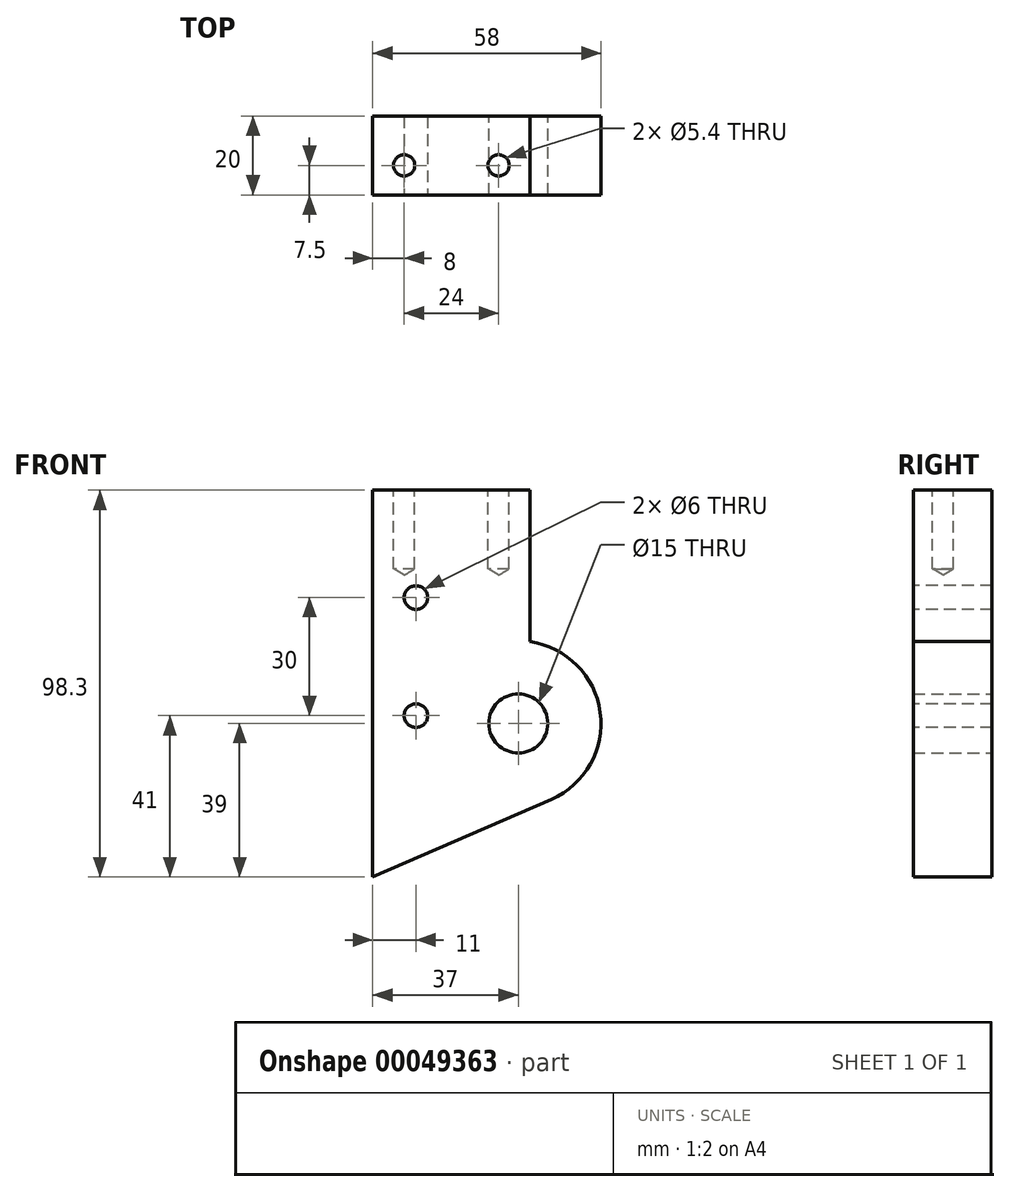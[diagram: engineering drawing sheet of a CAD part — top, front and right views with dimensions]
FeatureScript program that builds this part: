
annotation { "Feature Type Name" : "Feature", "Feature Type Description" : "" }
export const myFeature = defineFeature(function(context is Context, id is Id, definition is map)
    precondition{}
    {
        {
            var Q0;
            Q0=qCreatedBy(makeId("Front.planeOp"),FACE);
            var sketch = newSketch(context, id + "F0", { "sketchPlane" : qUnion([Q0])});
            skArc(sketch, "E0", {"start": v(8.38, -19.26) * mm, "mid": v(20.81, 2.8) * mm, "end": v(3, 20.78) * mm});
            skLineSegment(sketch, "E1", {"start": v(-37, 59.3) * mm, "end": v(3, 59.3) * mm});
            skLineSegment(sketch, "E2", {"start": v(3, 59.3) * mm, "end": v(3, 20.78) * mm});
            skLineSegment(sketch, "E3", {"start": v(-37, 59.3) * mm, "end": v(-37, -39) * mm});
            skLineSegment(sketch, "E4", {"start": v(-37, -39) * mm, "end": v(8.38, -19.26) * mm});
            skCircle(sketch, "E5", {"center": v(0, 0) * mm, "radius": 7.5 * mm});
            skSolve(sketch);
        }
        {
            var Q0;
            Q0=makeQuery(id+"F0.imprint","IMPRINT",FACE,{"disambiguationData":[TD([[makeQuery(id+"F0.imprint","IMPRINT",EDGE,{"derivedFrom":sQuery(id+"F0.wireOp",EDGE,"E0")}),1.0]])]});
            extrude(context, id + "F1", {"entities" : qUnion([Q0]), "depth" : 20 * mm});
        }
        {
            var Q0;
            Q0=makeQuery(id+"F1.opExtrude","SWEPT_FACE",FACE,{"disambiguationData":[OSD([sQuery(id+"F0.wireOp",EDGE,"E1")])]});
            var sketch = newSketch(context, id + "F2", { "sketchPlane" : qUnion([Q0])});
            skCircle(sketch, "E6", {"center": v(-29, -12.5) * mm, "radius": 2.7 * mm, "construction": true});
            skCircle(sketch, "E7", {"center": v(-5, -12.5) * mm, "radius": 2.7 * mm, "construction": true});
            skPoint(sketch, "E8.start.orphan", {"position": v(-17, -12.5) * mm});
            skLineSegment(sketch, "E9", {"start": v(-5, -12.5) * mm, "end": v(-29, -12.5) * mm, "construction": true});
            skLineSegment(sketch, "E10", {"start": v(-17, -12.5) * mm, "end": v(-17, -20) * mm, "construction": true});
            skSolve(sketch);
        }
        {
            var Q0;
            Q0=sQuery(id+"F2.wireOp",VERTEX,"E6.center");
            var Q1;
            Q1=sQuery(id+"F2.wireOp",VERTEX,"E7.center");
            var Q2;
            Q2=makeQuery(id+"F1.opExtrude","SWEPT_BODY",BODY,{"disambiguationData":[OSD([sQuery(id+"F0.wireOp",EDGE,"E0"),sQuery(id+"F0.wireOp",EDGE,"E1"),sQuery(id+"F0.wireOp",EDGE,"E2"),sQuery(id+"F0.wireOp",EDGE,"E3"),sQuery(id+"F0.wireOp",EDGE,"E4"),sQuery(id+"F0.wireOp",EDGE,"E5")])]});
            hole(context, id + "F3", {"style" : HoleStyle.SIMPLE, "holeDiameter" : 5.4 * mm, "endStyle" : HoleEndStyle.BLIND, "holeDepth" : 20 * mm, "locations" : qUnion([Q0, Q1]), "scope" : qUnion([Q2])});
        }
        {
            var Q0;
            Q0=makeQuery(id+"F1.opExtrude","CAP_FACE",FACE,{"disambiguationData":[OSD([sQuery(id+"F0.wireOp",EDGE,"E0"),sQuery(id+"F0.wireOp",EDGE,"E1"),sQuery(id+"F0.wireOp",EDGE,"E2"),sQuery(id+"F0.wireOp",EDGE,"E3"),sQuery(id+"F0.wireOp",EDGE,"E4"),sQuery(id+"F0.wireOp",EDGE,"E5")])],"isStart":false});
            var sketch = newSketch(context, id + "F4", { "sketchPlane" : qUnion([Q0])});
            skCircle(sketch, "E11", {"center": v(-26, 32) * mm, "radius": 3 * mm, "construction": true});
            skLineSegment(sketch, "E12", {"start": v(-26, 2) * mm, "end": v(-26, 32) * mm, "construction": true});
            skLineSegment(sketch, "E13", {"start": v(-26, 59.3) * mm, "end": v(-26, 32) * mm, "construction": true});
            skCircle(sketch, "E14", {"center": v(-26, 2) * mm, "radius": 3 * mm, "construction": true});
            skPoint(sketch, "E15.orphan", {"position": v(-26, 0) * mm});
            skSolve(sketch);
        }
        {
            var Q0;
            Q0=sQuery(id+"F4.wireOp",VERTEX,"E11.center");
            var Q1;
            Q1=sQuery(id+"F4.wireOp",VERTEX,"E14.center");
            var Q2;
            Q2=makeQuery(id+"F1.opExtrude","SWEPT_BODY",BODY,{"disambiguationData":[OSD([sQuery(id+"F0.wireOp",EDGE,"E0"),sQuery(id+"F0.wireOp",EDGE,"E1"),sQuery(id+"F0.wireOp",EDGE,"E2"),sQuery(id+"F0.wireOp",EDGE,"E3"),sQuery(id+"F0.wireOp",EDGE,"E4"),sQuery(id+"F0.wireOp",EDGE,"E5")])]});
            hole(context, id + "F5", {"style" : HoleStyle.SIMPLE, "holeDiameter" : 6 * mm, "endStyle" : HoleEndStyle.THROUGH, "locations" : qUnion([Q0, Q1]), "scope" : qUnion([Q2])});
        }
    });
